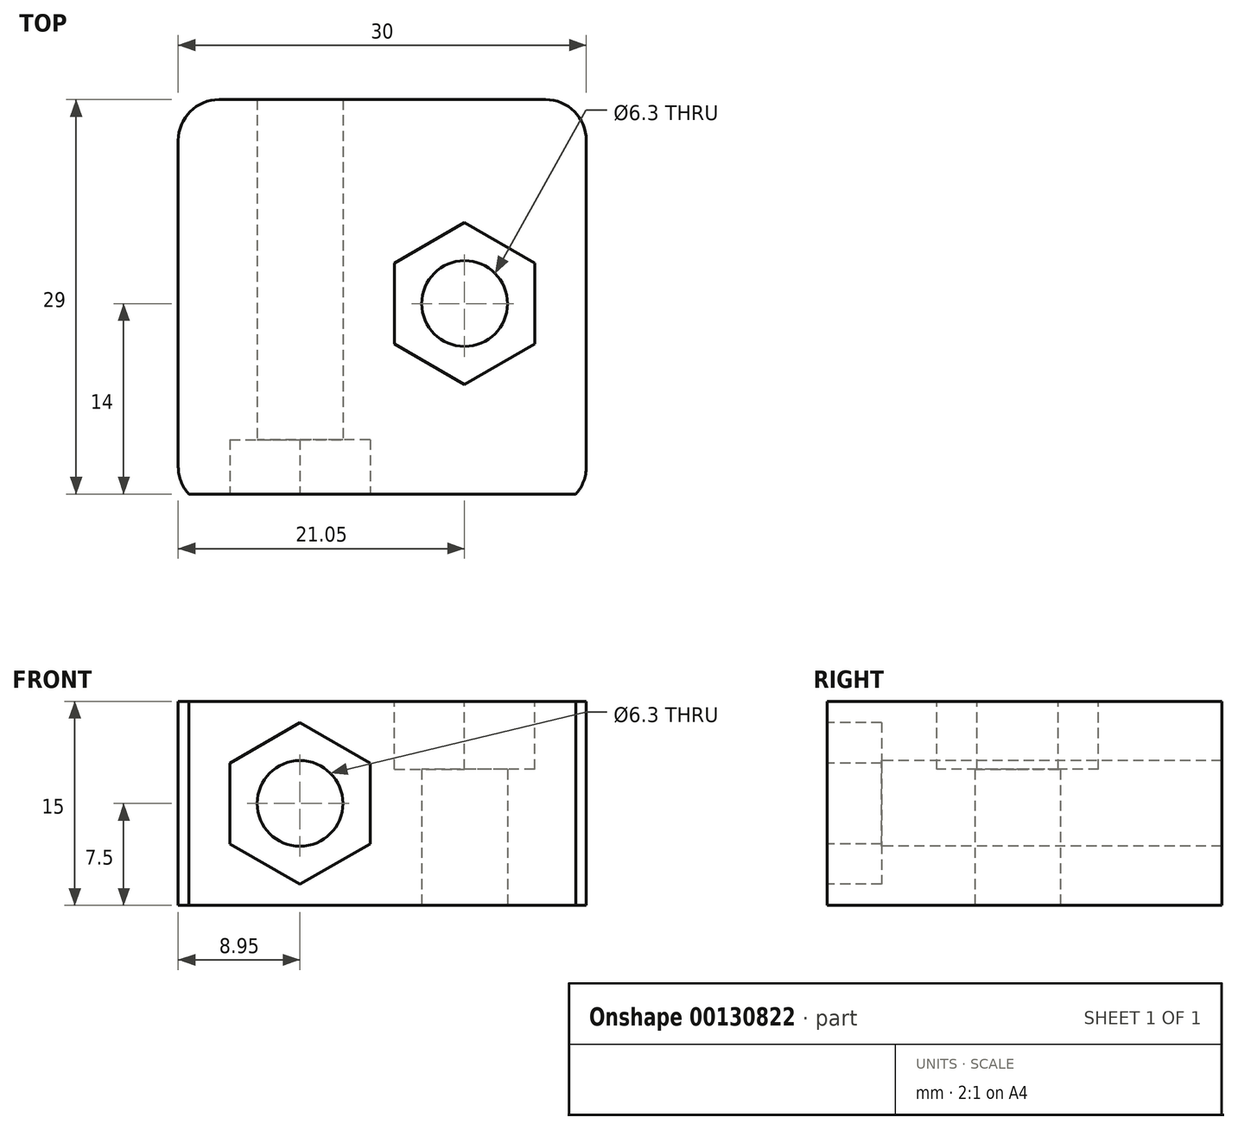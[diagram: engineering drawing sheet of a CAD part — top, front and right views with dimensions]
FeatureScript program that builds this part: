
annotation { "Feature Type Name" : "Feature", "Feature Type Description" : "" }
export const myFeature = defineFeature(function(context is Context, id is Id, definition is map)
    precondition{}
    {
        {
            assignVariable(context, id + "F0", {"name" : "x", "anyValue" : 30});
        }
        {
            assignVariable(context, id + "F1", {"name" : "NussTiefe", "anyValue" : 5});
        }
        {
            var Q0;
            Q0=qCreatedBy(makeId("Top.planeOp"),FACE);
            var sketch = newSketch(context, id + "F2", { "sketchPlane" : qUnion([Q0])});
            skLineSegment(sketch, "E0.bottom", {"start": v(15, -15) * mm, "end": v(-15, -15) * mm});
            skLineSegment(sketch, "E0.top", {"start": v(15, 15) * mm, "end": v(-15, 15) * mm});
            skLineSegment(sketch, "E0.left", {"start": v(15, -15) * mm, "end": v(15, 15) * mm});
            skLineSegment(sketch, "E0.right", {"start": v(-15, -15) * mm, "end": v(-15, 15) * mm});
            skPoint(sketch, "E0.middle", {"position": v(0, 0) * mm});
            skCircle(sketch, "E1", {"center": v(6.05, 0) * mm, "radius": 3.15 * mm});
            skSolve(sketch);
        }
        {
            var Q0;
            Q0 = qSketchRegion(id + "F2", true);
            extrude(context, id + "F3", {"entities" : qUnion([Q0]), "endBound" : BoundingType.SYMMETRIC, "depth" : (getVariable(context, 'x') / 2) * mm});
        }
        {
            var Q0;
            Q0=makeQuery(id+"F3.opExtrude","SWEPT_FACE",FACE,{"disambiguationData":[OSD([sQuery(id+"F2.wireOp",EDGE,"E0.bottom")])]});
            var sketch = newSketch(context, id + "F4", { "sketchPlane" : qUnion([Q0])});
            skCircle(sketch, "E2", {"center": v(-6.05, 0) * mm, "radius": 3.15 * mm});
            skCircle(sketch, "E3.cCircle", {"center": v(-6.05, 0) * mm, "radius": 5.15 * mm, "construction": true});
            skLineSegment(sketch, "E3.0", {"start": v(-0.9, -2.97) * mm, "end": v(-6.05, -5.95) * mm});
            skLineSegment(sketch, "E3.1", {"start": v(-6.05, -5.95) * mm, "end": v(-11.2, -2.97) * mm});
            skLineSegment(sketch, "E3.2", {"start": v(-11.2, -2.97) * mm, "end": v(-11.2, 2.97) * mm});
            skLineSegment(sketch, "E3.3", {"start": v(-11.2, 2.97) * mm, "end": v(-6.05, 5.95) * mm});
            skLineSegment(sketch, "E3.4", {"start": v(-6.05, 5.95) * mm, "end": v(-0.9, 2.97) * mm});
            skLineSegment(sketch, "E3.5", {"start": v(-0.9, 2.97) * mm, "end": v(-0.9, -2.97) * mm});
            skPoint(sketch, "E3.0.midPoint", {"position": v(-3.48, -4.46) * mm});
            skSolve(sketch);
        }
        {
            var Q0;
            Q0=makeQuery(id+"F4.imprint","IMPRINT",FACE,{"disambiguationData":[TD([[makeQuery(id+"F4.imprint","IMPRINT",EDGE,{"derivedFrom":sQuery(id+"F4.wireOp",EDGE,"E2")}),1.0]])]});
            extrude(context, id + "F5", {"entities" : qUnion([Q0]), "operationType" : NewBodyOperationType.REMOVE, "endBound" : BoundingType.UP_TO_NEXT, "oppositeDirection" : true, "depth" : 25 * mm});
        }
        {
            var Q0;
            Q0=makeQuery(id+"F3.opExtrude","CAP_FACE",FACE,{"disambiguationData":[OSD([sQuery(id+"F2.wireOp",EDGE,"E0.bottom"),sQuery(id+"F2.wireOp",EDGE,"E0.top"),sQuery(id+"F2.wireOp",EDGE,"E0.left"),sQuery(id+"F2.wireOp",EDGE,"E0.right"),sQuery(id+"F2.wireOp",EDGE,"E1")])],"isStart":false});
            var sketch = newSketch(context, id + "F6", { "sketchPlane" : qUnion([Q0])});
            skCircle(sketch, "E4.cCircle", {"center": v(6.05, 0) * mm, "radius": 5.15 * mm, "construction": true});
            skLineSegment(sketch, "E4.0", {"start": v(11.2, -2.97) * mm, "end": v(6.05, -5.95) * mm});
            skLineSegment(sketch, "E4.1", {"start": v(6.05, -5.95) * mm, "end": v(0.9, -2.97) * mm});
            skLineSegment(sketch, "E4.2", {"start": v(0.9, -2.97) * mm, "end": v(0.9, 2.97) * mm});
            skLineSegment(sketch, "E4.3", {"start": v(0.9, 2.97) * mm, "end": v(6.05, 5.95) * mm});
            skLineSegment(sketch, "E4.4", {"start": v(6.05, 5.95) * mm, "end": v(11.2, 2.97) * mm});
            skLineSegment(sketch, "E4.5", {"start": v(11.2, 2.97) * mm, "end": v(11.2, -2.97) * mm});
            skPoint(sketch, "E4.0.midPoint", {"position": v(8.62, -4.46) * mm});
            skSolve(sketch);
        }
        {
            var Q0;
            Q0=makeQuery(id+"F3.opExtrude","SWEPT_EDGE",EDGE,{"disambiguationData":[OSD([sQuery(id+"F2.wireOp",EDGE,"E0.bottom"),sQuery(id+"F2.wireOp",EDGE,"E0.right")])]});
            var Q1;
            Q1=makeQuery(id+"F3.opExtrude","SWEPT_EDGE",EDGE,{"disambiguationData":[OSD([sQuery(id+"F2.wireOp",EDGE,"E0.bottom"),sQuery(id+"F2.wireOp",EDGE,"E0.left")])]});
            var Q2;
            Q2=makeQuery(id+"F3.opExtrude","SWEPT_EDGE",EDGE,{"disambiguationData":[OSD([sQuery(id+"F2.wireOp",EDGE,"E0.top"),sQuery(id+"F2.wireOp",EDGE,"E0.left")])]});
            var Q3;
            Q3=makeQuery(id+"F3.opExtrude","SWEPT_EDGE",EDGE,{"disambiguationData":[OSD([sQuery(id+"F2.wireOp",EDGE,"E0.top"),sQuery(id+"F2.wireOp",EDGE,"E0.right")])]});
            fillet(context, id + "F7", {"entities" : qUnion([Q0, Q1, Q2, Q3]), "radius" : 3 * mm, "tangentPropagation" : true, "allowEdgeOverflow" : false});
        }
        {
            var Q0;
            Q0=makeQuery(id+"F4.imprint","IMPRINT",FACE,{"disambiguationData":[TD([[makeQuery(id+"F4.imprint","IMPRINT",EDGE,{"derivedFrom":sQuery(id+"F4.wireOp",EDGE,"E2")}),-1.0]])]});
            extrude(context, id + "F8", {"entities" : qUnion([Q0]), "operationType" : NewBodyOperationType.REMOVE, "oppositeDirection" : true, "depth" : (getVariable(context, 'NussTiefe')) * mm});
        }
        {
            var Q0;
            Q0=makeQuery(id+"F6.imprint","IMPRINT",FACE,{"disambiguationData":[TD([[makeQuery(id+"F6.imprint","IMPRINT",EDGE,{"derivedFrom":sQuery(id+"F6.wireOp",EDGE,"E4.0")}),-1.0]])]});
            extrude(context, id + "F9", {"entities" : qUnion([Q0]), "operationType" : NewBodyOperationType.REMOVE, "oppositeDirection" : true, "depth" : (getVariable(context, 'NussTiefe')) * mm});
        }
        {
            var Q0;
            Q0=makeQuery(id+"F4.imprint","IMPRINT",FACE,{"disambiguationData":[TD([[makeQuery(id+"F4.imprint","IMPRINT",EDGE,{"derivedFrom":sQuery(id+"F4.wireOp",EDGE,"E3.0")}),1.0]])]});
            var sketch = newSketch(context, id + "F10", { "sketchPlane" : qUnion([Q0])});
            skText(sketch, "E5", { "text": "R", "fontName": "OpenSans-Bold.ttf"});
            skPoint(sketch, "E6", {"position": v(1.38, 0) * mm});
            skLineSegment(sketch, "E7", {"start": v(1.38, -3.97) * mm, "end": v(9.38, -3.97) * mm});
            const initialGuessF10  = {"E5": [0.00138, -0.00397, 1, 0, 0.00794]};
            skSetInitialGuess(sketch, initialGuessF10);
            skSolve(sketch);
        }
        {
            var Q0;
            Q0=makeQuery(id+"F10.imprint","IMPRINT",FACE,{"disambiguationData":[TD([[makeQuery(id+"F10.imprint","IMPRINT",EDGE,{"derivedFrom":sQuery(id+"F10.wireOp",EDGE,"E5.sketch_text.stroke-0")}),1.0]])]});
            var Q1;
            Q1=makeQuery(id+"F10.imprint","IMPRINT",FACE,{"disambiguationData":[TD([[makeQuery(id+"F10.imprint","IMPRINT",EDGE,{"derivedFrom":sQuery(id+"F10.wireOp",EDGE,"E5.sketch_text.stroke-0")}),-1.0]])]});
            var Q2;
            {var subQ0=sQuery(id+"F10.wireOp",EDGE,"E5.sketch_text.stroke-7");Q2=makeQuery(id+"F10.imprint","IMPRINT",FACE,{"disambiguationData":[TD([[makeQuery(id+"F10.imprint","IMPRINT",EDGE,{"derivedFrom":subQ0}),1.0]])]});}
            extrude(context, id + "F11", {"entities" : qUnion([Q0, Q1, Q2]), "operationType" : NewBodyOperationType.REMOVE, "oppositeDirection" : true, "depth" : 1 * mm});
        }
    });
